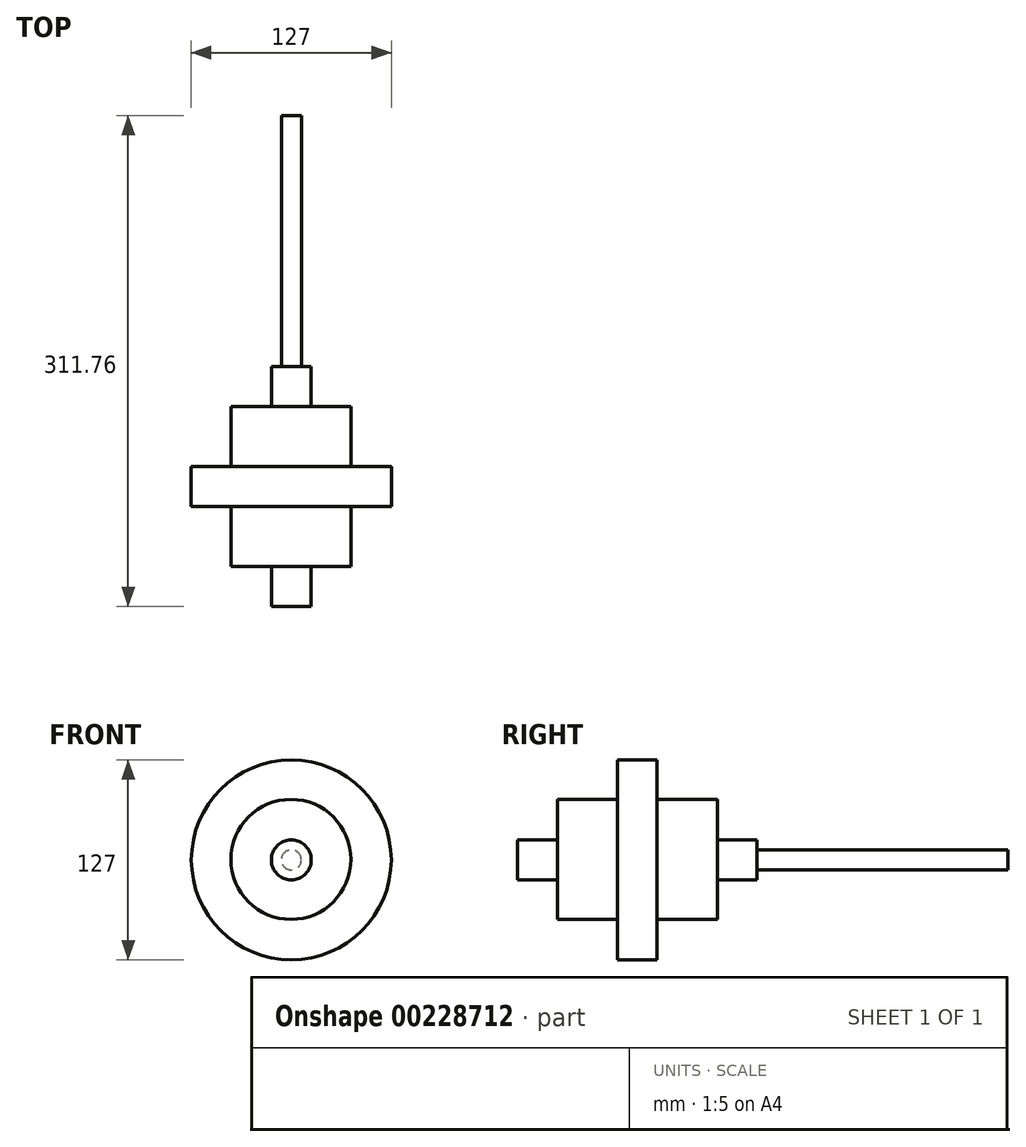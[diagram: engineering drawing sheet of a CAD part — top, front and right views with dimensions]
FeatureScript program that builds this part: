
annotation { "Feature Type Name" : "Feature", "Feature Type Description" : "" }
export const myFeature = defineFeature(function(context is Context, id is Id, definition is map)
    precondition{}
    {
        {
            var Q0;
            Q0=qCreatedBy(makeId("Front.planeOp"),FACE);
            var sketch = newSketch(context, id + "F0", { "sketchPlane" : qUnion([Q0])});
            skCircle(sketch, "E0", {"center": v(0, 0) * mm, "radius": 63.5 * mm});
            skSolve(sketch);
        }
        {
            var Q0;
            Q0=qCreatedBy(makeId("Front.planeOp"),FACE);
            var sketch = newSketch(context, id + "F1", { "sketchPlane" : qUnion([Q0])});
            skCircle(sketch, "E1", {"center": v(-0.21, 0.32) * mm, "radius": 38.1 * mm});
            skSolve(sketch);
        }
        {
            var Q0;
            Q0=qCreatedBy(makeId("Front.planeOp"),FACE);
            var sketch = newSketch(context, id + "F2", { "sketchPlane" : qUnion([Q0])});
            skCircle(sketch, "E2", {"center": v(0, 0) * mm, "radius": 12.7 * mm});
            skSolve(sketch);
        }
        {
            var Q0;
            Q0 = qSketchRegion(id + "F2", true);
            extrude(context, id + "F3", {"entities" : qUnion([Q0]), "endBound" : BoundingType.SYMMETRIC, "depth" : 152.4 * mm});
        }
        {
            var Q0;
            Q0 = qSketchRegion(id + "F1", true);
            extrude(context, id + "F4", {"entities" : qUnion([Q0]), "operationType" : NewBodyOperationType.ADD, "endBound" : BoundingType.SYMMETRIC, "depth" : 101.6 * mm});
        }
        {
            var Q0;
            Q0 = qSketchRegion(id + "F0", true);
            extrude(context, id + "F5", {"entities" : qUnion([Q0]), "operationType" : NewBodyOperationType.ADD, "endBound" : BoundingType.SYMMETRIC, "depth" : 25.4 * mm});
        }
        {
            var Q0;
            Q0=qCreatedBy(makeId("Front.planeOp"),FACE);
            var sketch = newSketch(context, id + "F6", { "sketchPlane" : qUnion([Q0])});
            skCircle(sketch, "E3", {"center": v(0, 0) * mm, "radius": 6.35 * mm});
            skSolve(sketch);
        }
        {
            var Q0;
            Q0 = qSketchRegion(id + "F6", true);
            extrude(context, id + "F7", {"entities" : qUnion([Q0]), "operationType" : NewBodyOperationType.ADD, "endBound" : BoundingType.THROUGH_ALL, "oppositeDirection" : true, "depth" : 25.4 * mm});
        }
    });
